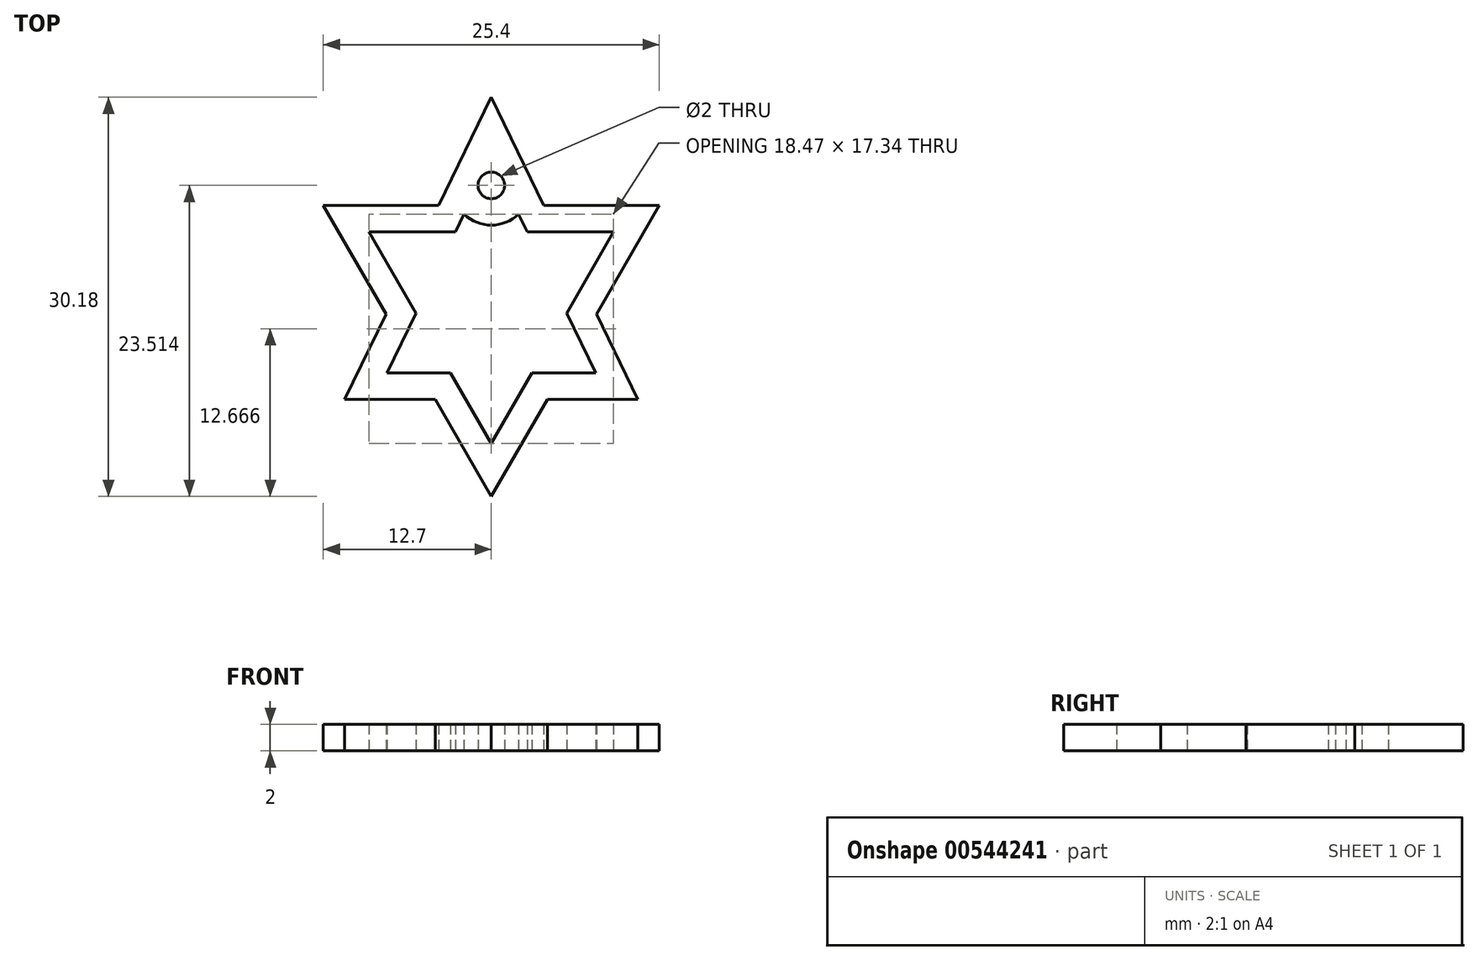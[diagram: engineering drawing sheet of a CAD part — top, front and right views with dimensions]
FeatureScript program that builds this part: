
annotation { "Feature Type Name" : "Feature", "Feature Type Description" : "" }
export const myFeature = defineFeature(function(context is Context, id is Id, definition is map)
    precondition{}
    {
        {
            var Q0;
            Q0=qCreatedBy(makeId("Top.planeOp"),FACE);
            var sketch = newSketch(context, id + "F0", { "sketchPlane" : qUnion([Q0])});
            skArc(sketch, "E0.cCircle", {"start": v(5.03, 5.33) * mm, "mid": v(0, 7.33) * mm, "end": v(-5.03, 5.33) * mm, "construction": true});
            skLineSegment(sketch, "E0.0", {"start": v(-12.7, 7.33) * mm, "end": v(12.7, 7.33) * mm});
            skLineSegment(sketch, "E0.1", {"start": v(12.7, 7.33) * mm, "end": v(6.75, -2.98) * mm});
            skLineSegment(sketch, "E0.2", {"start": v(0, -14.66) * mm, "end": v(-12.7, 7.33) * mm});
            skPoint(sketch, "E0.0.midPoint", {"position": v(0, 7.33) * mm});
            skLineSegment(sketch, "E1.0", {"start": v(-9.24, 5.33) * mm, "end": v(9.24, 5.33) * mm});
            skLineSegment(sketch, "E1.1", {"start": v(0, -10.66) * mm, "end": v(-3.08, -5.33) * mm});
            skLineSegment(sketch, "E1.2", {"start": v(9.24, 5.33) * mm, "end": v(5.7, -0.8) * mm});
            skLineSegment(sketch, "E2", {"start": v(-11.08, -7.33) * mm, "end": v(11.08, -7.33) * mm});
            skLineSegment(sketch, "E3", {"start": v(-11.08, -7.33) * mm, "end": v(-6.9, 1.29) * mm});
            skLineSegment(sketch, "E4", {"start": v(0, 15.52) * mm, "end": v(4.94, 5.33) * mm});
            skLineSegment(sketch, "E5.0", {"start": v(-7.89, -5.33) * mm, "end": v(-5.7, -0.8) * mm});
            skLineSegment(sketch, "E5.1", {"start": v(-7.89, -5.33) * mm, "end": v(-3.08, -5.33) * mm});
            skLineSegment(sketch, "E5.2", {"start": v(1, 8.87) * mm, "end": v(2.72, 5.33) * mm});
            skArc(sketch, "E6", {"start": v(-2.07, 6.68) * mm, "mid": v(0, 5.85) * mm, "end": v(2.07, 6.68) * mm});
            skArc(sketch, "E7.0", {"start": v(1, 8.87) * mm, "mid": v(0, 9.86) * mm, "end": v(-1, 8.87) * mm});
            skLineSegment(sketch, "E8.trimOffspring", {"start": v(5.7, -0.8) * mm, "end": v(7.89, -5.33) * mm});
            skLineSegment(sketch, "E9.trimOffspring", {"start": v(3.08, -5.33) * mm, "end": v(7.89, -5.33) * mm});
            skLineSegment(sketch, "E10.trimOffspring", {"start": v(6.9, 1.29) * mm, "end": v(11.08, -7.33) * mm});
            skLineSegment(sketch, "E11.trimOffspring", {"start": v(-2.72, 5.33) * mm, "end": v(-1, 8.87) * mm});
            skLineSegment(sketch, "E12.trimOffspring", {"start": v(-4.94, 5.33) * mm, "end": v(0, 15.52) * mm});
            skLineSegment(sketch, "E13.trimOffspring", {"start": v(-5.7, -0.8) * mm, "end": v(-9.24, 5.33) * mm});
            skArc(sketch, "E14.trimOffspring", {"start": v(-7.13, 1.7) * mm, "mid": v(-7.26, -1.06) * mm, "end": v(-6.35, -3.67) * mm, "construction": true});
            skLineSegment(sketch, "E15.trimOffspring", {"start": v(3.08, -5.33) * mm, "end": v(0, -10.66) * mm});
            skArc(sketch, "E16.trimOffspring", {"start": v(6.72, -2.93) * mm, "mid": v(7.3, -0.65) * mm, "end": v(7.13, 1.7) * mm, "construction": true});
            skLineSegment(sketch, "E17.trimOffspring", {"start": v(5.39, -5.33) * mm, "end": v(0, -14.66) * mm});
            skArc(sketch, "E18.trimOffspring", {"start": v(-5.03, -5.33) * mm, "mid": v(0, -7.33) * mm, "end": v(5.03, -5.33) * mm, "construction": true});
            skArc(sketch, "E19", {"start": v(-1, 8.87) * mm, "mid": v(0, 7.85) * mm, "end": v(1, 8.87) * mm});
            skSolve(sketch);
        }
        {
            var Q0;
            {var subQ1=sQuery(id+"F0.wireOp",EDGE,"E7.0");Q0=makeQuery(id+"F0.imprint","IMPRINT",FACE,{"disambiguationData":[TD([[makeQuery(id+"F0.imprint","IMPRINT",EDGE,{"derivedFrom":subQ1}),-1.0]])]});}
            var Q1;
            {var subQ5=sQuery(id+"F0.wireOp",EDGE,"E6");Q1=makeQuery(id+"F0.imprint","IMPRINT",FACE,{"disambiguationData":[TD([[makeQuery(id+"F0.imprint","IMPRINT",EDGE,{"derivedFrom":subQ5}),1.0]])]});}
            var Q2;
            {var subQ3=sQuery(id+"F0.wireOp",EDGE,"E0.2");var subQ9=sQuery(id+"F0.wireOp",EDGE,"E0.0");var subQ10=makeQuery(id+"F0.imprint","INTERSECT",VERTEX,{"derivedFrom":[subQ9,subQ3]});Q2=makeQuery(id+"F0.imprint","IMPRINT",FACE,{"disambiguationData":[TD([[makeQuery(id+"F0.imprint","IMPRINT",EDGE,{"disambiguationData":[TD([[subQ10,-1.0]])],"derivedFrom":subQ9}),-1.0]])]});}
            var Q3;
            {var subQ4=sQuery(id+"F0.wireOp",EDGE,"E12.trimOffspring");var subQ5=sQuery(id+"F0.wireOp",EDGE,"E0.0");var subQ6=makeQuery(id+"F0.imprint","INTERSECT",VERTEX,{"derivedFrom":[subQ5,subQ4]});Q3=makeQuery(id+"F0.imprint","IMPRINT",FACE,{"disambiguationData":[TD([[makeQuery(id+"F0.imprint","IMPRINT",EDGE,{"disambiguationData":[TD([[subQ6,-1.0]])],"derivedFrom":subQ5}),-1.0]])]});}
            var Q4;
            {var subQ5=sQuery(id+"F0.wireOp",EDGE,"E0.1");var subQ6=sQuery(id+"F0.wireOp",EDGE,"E0.0");var subQ7=makeQuery(id+"F0.imprint","INTERSECT",VERTEX,{"derivedFrom":[subQ6,subQ5]});Q4=makeQuery(id+"F0.imprint","IMPRINT",FACE,{"disambiguationData":[TD([[makeQuery(id+"F0.imprint","IMPRINT",EDGE,{"disambiguationData":[TD([[subQ7,1.0]])],"derivedFrom":subQ6}),-1.0]])]});}
            var Q5;
            {var subQ0=sQuery(id+"F0.wireOp",EDGE,"E4");var subQ3=sQuery(id+"F0.wireOp",EDGE,"E0.0");var subQ4=makeQuery(id+"F0.imprint","INTERSECT",VERTEX,{"derivedFrom":[subQ3,subQ0]});Q5=makeQuery(id+"F0.imprint","IMPRINT",FACE,{"disambiguationData":[TD([[makeQuery(id+"F0.imprint","IMPRINT",EDGE,{"disambiguationData":[TD([[subQ4,1.0]])],"derivedFrom":subQ3}),-1.0]])]});}
            var Q6;
            {var subQ0=sQuery(id+"F0.wireOp",EDGE,"E3");var subQ1=sQuery(id+"F0.wireOp",EDGE,"E0.2");var subQ2=makeQuery(id+"F0.imprint","INTERSECT",VERTEX,{"derivedFrom":[subQ1,subQ0]});Q6=makeQuery(id+"F0.imprint","IMPRINT",FACE,{"disambiguationData":[TD([[makeQuery(id+"F0.imprint","IMPRINT",EDGE,{"disambiguationData":[TD([[subQ2,1.0]])],"derivedFrom":subQ1}),-1.0]])]});}
            var Q7;
            {var subQ1=sQuery(id+"F0.wireOp",EDGE,"E2");var subQ3=sQuery(id+"F0.wireOp",EDGE,"E0.2");var subQ5=makeQuery(id+"F0.imprint","INTERSECT",VERTEX,{"derivedFrom":[subQ3,subQ1]});Q7=makeQuery(id+"F0.imprint","IMPRINT",FACE,{"disambiguationData":[TD([[makeQuery(id+"F0.imprint","IMPRINT",EDGE,{"disambiguationData":[TD([[subQ5,-1.0]])],"derivedFrom":subQ3}),1.0]])]});}
            var Q8;
            {var subQ0=sQuery(id+"F0.wireOp",EDGE,"E2");var subQ1=sQuery(id+"F0.wireOp",EDGE,"E0.2");var subQ2=makeQuery(id+"F0.imprint","INTERSECT",VERTEX,{"derivedFrom":[subQ1,subQ0]});Q8=makeQuery(id+"F0.imprint","IMPRINT",FACE,{"disambiguationData":[TD([[makeQuery(id+"F0.imprint","IMPRINT",EDGE,{"disambiguationData":[TD([[subQ2,-1.0]])],"derivedFrom":subQ1}),-1.0]])]});}
            var Q9;
            {var subQ0=sQuery(id+"F0.wireOp",EDGE,"E17.trimOffspring");var subQ5=sQuery(id+"F0.wireOp",EDGE,"E0.2");var subQ9=makeQuery(id+"F0.imprint","INTERSECT",VERTEX,{"derivedFrom":[subQ5,subQ0]});Q9=makeQuery(id+"F0.imprint","IMPRINT",FACE,{"disambiguationData":[TD([[makeQuery(id+"F0.imprint","IMPRINT",EDGE,{"disambiguationData":[TD([[subQ9,-1.0]])],"derivedFrom":subQ5}),-1.0]])]});}
            var Q10;
            {var subQ0=sQuery(id+"F0.wireOp",EDGE,"E17.trimOffspring");var subQ1=sQuery(id+"F0.wireOp",EDGE,"E2");var subQ2=makeQuery(id+"F0.imprint","INTERSECT",VERTEX,{"derivedFrom":[subQ1,subQ0]});Q10=makeQuery(id+"F0.imprint","IMPRINT",FACE,{"disambiguationData":[TD([[makeQuery(id+"F0.imprint","IMPRINT",EDGE,{"disambiguationData":[TD([[subQ2,1.0]])],"derivedFrom":subQ1}),1.0]])]});}
            var Q11;
            {var subQ1=sQuery(id+"F0.wireOp",EDGE,"E8.trimOffspring");var subQ5=sQuery(id+"F0.wireOp",EDGE,"E0.1");var subQ6=makeQuery(id+"F0.imprint","INTERSECT",VERTEX,{"derivedFrom":[subQ5,subQ1]});Q11=makeQuery(id+"F0.imprint","IMPRINT",FACE,{"disambiguationData":[TD([[makeQuery(id+"F0.imprint","IMPRINT",EDGE,{"disambiguationData":[TD([[subQ6,1.0]])],"derivedFrom":subQ5}),1.0]])]});}
            var Q12;
            {var subQ0=sQuery(id+"F0.wireOp",EDGE,"E8.trimOffspring");var subQ1=sQuery(id+"F0.wireOp",EDGE,"E0.1");var subQ2=makeQuery(id+"F0.imprint","INTERSECT",VERTEX,{"derivedFrom":[subQ1,subQ0]});Q12=makeQuery(id+"F0.imprint","IMPRINT",FACE,{"disambiguationData":[TD([[makeQuery(id+"F0.imprint","IMPRINT",EDGE,{"disambiguationData":[TD([[subQ2,1.0]])],"derivedFrom":subQ1}),-1.0]])]});}
            var Q13;
            {var subQ5=sQuery(id+"F0.wireOp",EDGE,"E19");Q13=makeQuery(id+"F0.imprint","IMPRINT",FACE,{"disambiguationData":[TD([[makeQuery(id+"F0.imprint","IMPRINT",EDGE,{"derivedFrom":subQ5}),-1.0]])]});}
            extrude(context, id + "F1", {"entities" : qUnion([Q0, Q1, Q2, Q3, Q4, Q5, Q6, Q7, Q8, Q9, Q10, Q11, Q12, Q13]), "depth" : 2 * mm, "offsetDistance" : 25.4 * mm});
        }
    });
